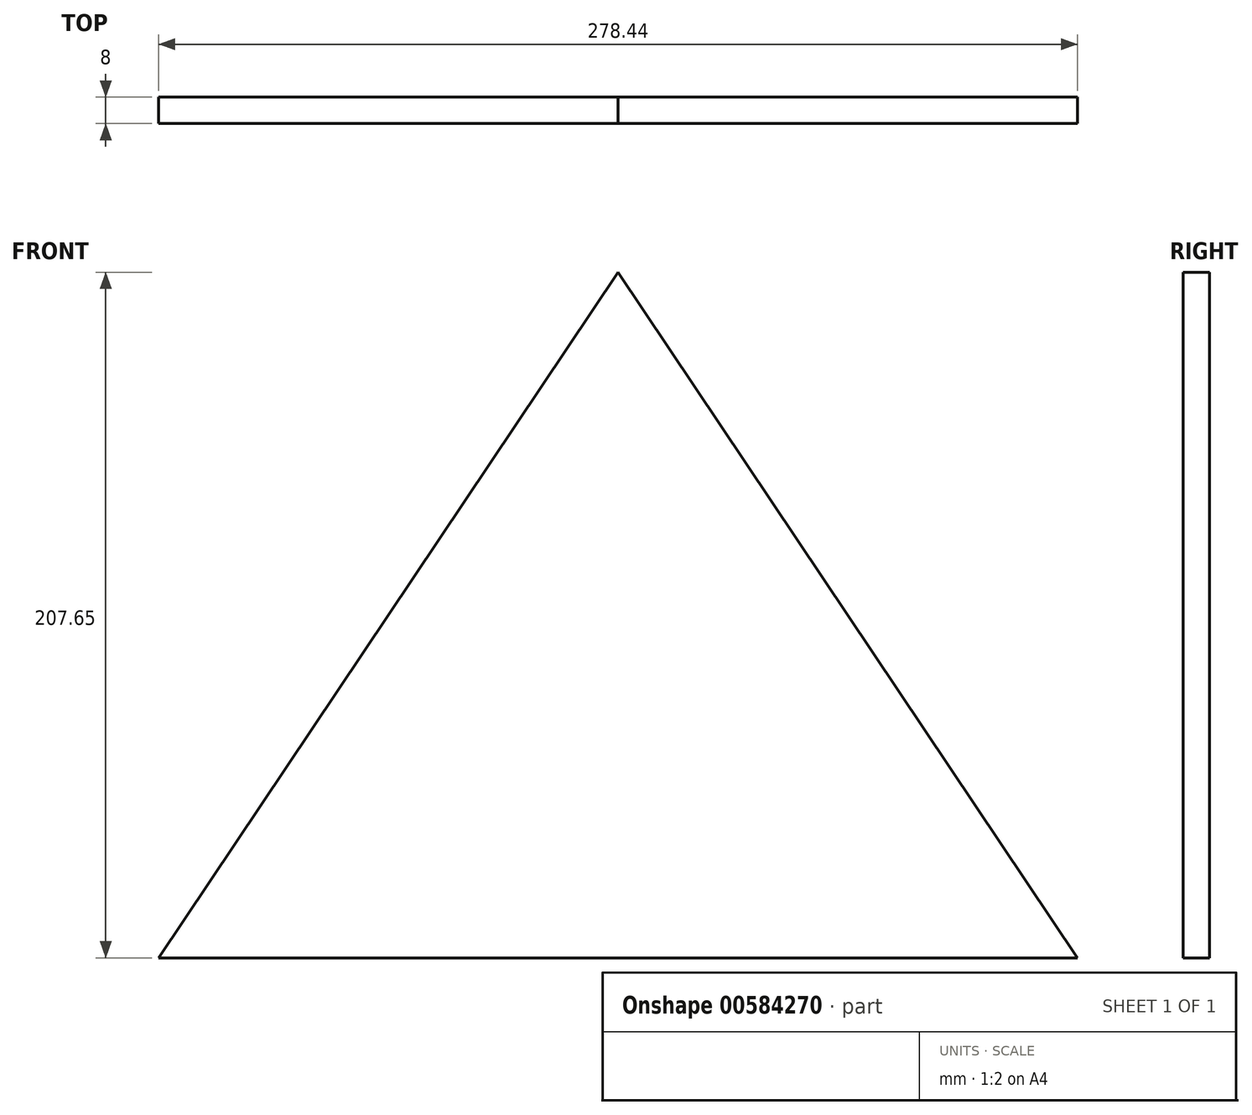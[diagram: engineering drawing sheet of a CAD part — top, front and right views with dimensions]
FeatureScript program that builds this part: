
annotation { "Feature Type Name" : "Feature", "Feature Type Description" : "" }
export const myFeature = defineFeature(function(context is Context, id is Id, definition is map)
    precondition{}
    {
        {
            var Q0;
            Q0=qCreatedBy(makeId("Front.planeOp"),FACE);
            var sketch = newSketch(context, id + "F0", { "sketchPlane" : qUnion([Q0])});
            skLineSegment(sketch, "E0", {"start": v(0, 0) * mm, "end": v(278.44, 0) * mm});
            skLineSegment(sketch, "E1", {"start": v(278.44, 0) * mm, "end": v(139.22, 207.65) * mm});
            skLineSegment(sketch, "E2", {"start": v(139.22, 207.65) * mm, "end": v(0, 0) * mm});
            skSolve(sketch);
        }
        {
            var Q0;
            Q0=makeQuery(id+"F0.imprint","IMPRINT",FACE,{"disambiguationData":[TD([[makeQuery(id+"F0.imprint","IMPRINT",EDGE,{"derivedFrom":sQuery(id+"F0.wireOp",EDGE,"E0")}),1.0]])]});
            extrude(context, id + "F1", {"entities" : qUnion([Q0]), "depth" : 8 * mm, "offsetDistance" : 25 * mm});
        }
    });
